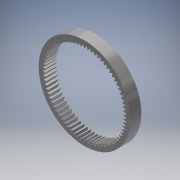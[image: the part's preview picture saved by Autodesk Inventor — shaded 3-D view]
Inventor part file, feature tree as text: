
AUTODESK INVENTOR PART (.ipt)
format: ipt  version: 2019 (Build 230136000, 136)  size: 462,848 bytes
history: native  units: mm (DEFAULTED — no unit token found)
features: plane x3, other x3, sketch x2, extrude x1
ambient origin geometry x8: Origin, YZ Plane, XZ Plane, XY Plane, X Axis, Y Axis, Z Axis, Center Point
bodies: Solid1 (feature_tree)
feature tree (9):
  extrude  "Extrusion1"  Depth=15.0mm TaperAngle=0.0deg
  plane  "Work Plane2"
  plane  "Work Plane8"
  plane  "Work Plane9"
  other  "正齒輪"
  sketch  "Sketch1"  dims[d0=123.430444mm d1=15.0mm d2=0.0mm]
  sketch  "Sketch2"  dims[d3=107.919785mm d4=10.0mm d5=0.0mm d16=37.698007mm d17=0.0mm d34=0.430355mm d39=0.0mm d45=0.0mm d47=37.698007mm d50=0.0mm d51=0.0mm d52=37.698007mm]
  other  "Srf1"
  other  "節圓直徑"
